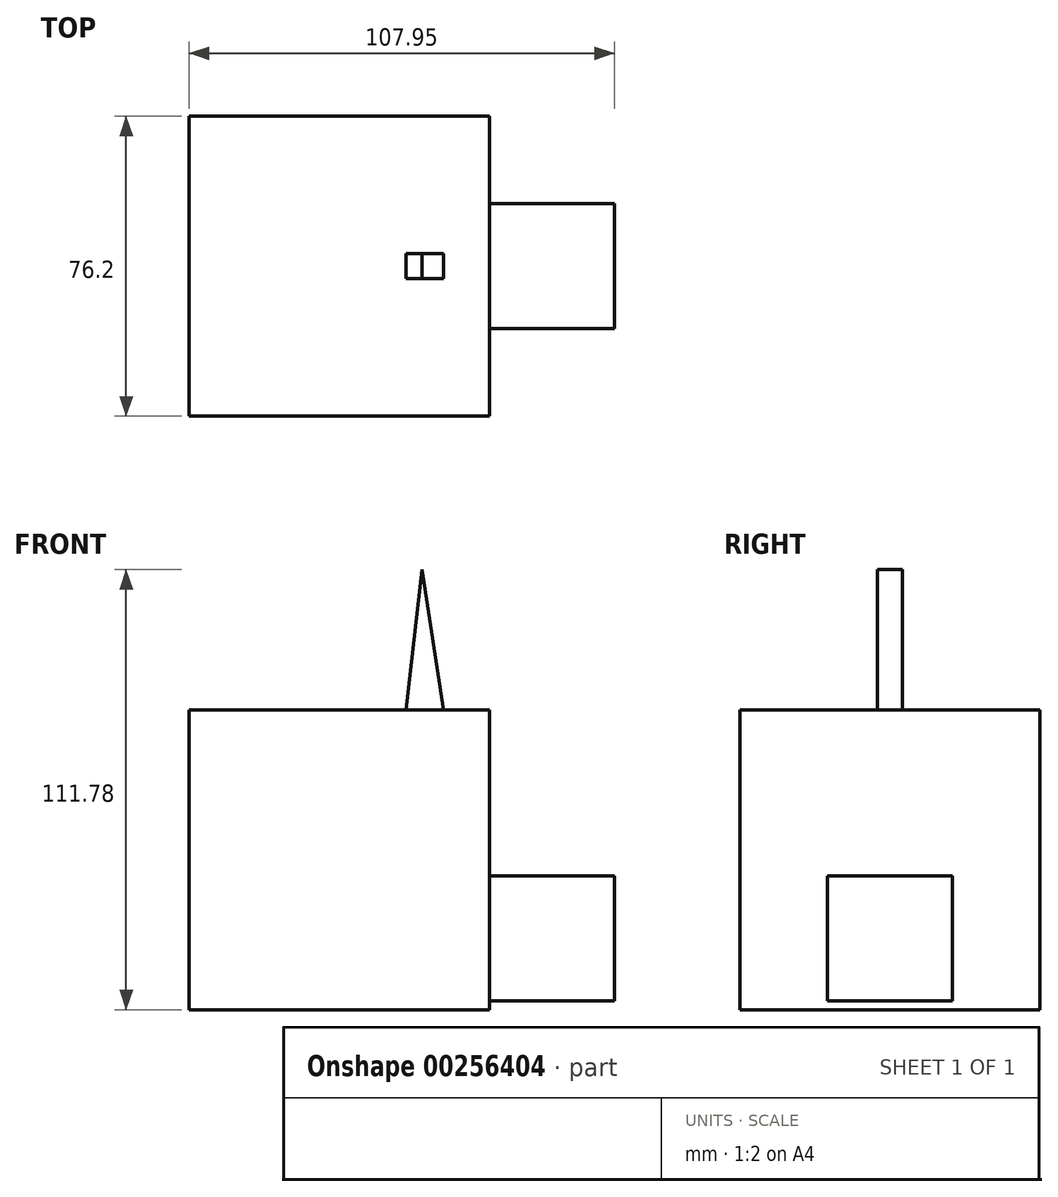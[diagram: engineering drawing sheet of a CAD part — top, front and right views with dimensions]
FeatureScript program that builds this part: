
annotation { "Feature Type Name" : "Feature", "Feature Type Description" : "" }
export const myFeature = defineFeature(function(context is Context, id is Id, definition is map)
    precondition{}
    {
        {
            var Q0;
            Q0=qCreatedBy(makeId("Front.planeOp"),FACE);
            var sketch = newSketch(context, id + "F0", { "sketchPlane" : qUnion([Q0])});
            skLineSegment(sketch, "E0.bottom", {"start": v(38.1, -38.1) * mm, "end": v(-38.1, -38.1) * mm});
            skLineSegment(sketch, "E0.top", {"start": v(38.1, 38.1) * mm, "end": v(-38.1, 38.1) * mm});
            skLineSegment(sketch, "E0.left", {"start": v(38.1, -38.1) * mm, "end": v(38.1, 38.1) * mm});
            skLineSegment(sketch, "E0.right", {"start": v(-38.1, -38.1) * mm, "end": v(-38.1, 38.1) * mm});
            skPoint(sketch, "E0.middle", {"position": v(0, 0) * mm});
            skLineSegment(sketch, "E1", {"start": v(16.94, 38.1) * mm, "end": v(21.02, 73.68) * mm});
            skLineSegment(sketch, "E2", {"start": v(21.02, 73.68) * mm, "end": v(26.53, 38.1) * mm});
            skLineSegment(sketch, "E3.bottom", {"start": v(38.1, -4.17) * mm, "end": v(69.85, -4.17) * mm});
            skLineSegment(sketch, "E3.top", {"start": v(38.1, -35.92) * mm, "end": v(69.85, -35.92) * mm});
            skLineSegment(sketch, "E3.left", {"start": v(38.1, -4.17) * mm, "end": v(38.1, -35.92) * mm});
            skLineSegment(sketch, "E3.right", {"start": v(69.85, -4.17) * mm, "end": v(69.85, -35.92) * mm});
            skSolve(sketch);
        }
        {
            var Q0;
            {var subQ6=sQuery(id+"F0.wireOp",EDGE,"E0.bottom");Q0=makeQuery(id+"F0.imprint","IMPRINT",FACE,{"disambiguationData":[TD([[makeQuery(id+"F0.imprint","IMPRINT",EDGE,{"derivedFrom":subQ6}),-1.0]])]});}
            extrude(context, id + "F1", {"entities" : qUnion([Q0]), "endBound" : BoundingType.SYMMETRIC, "depth" : 76.2 * mm});
        }
        {
            var Q0;
            Q0=makeQuery(id+"F0.imprint","IMPRINT",FACE,{"disambiguationData":[TD([[makeQuery(id+"F0.imprint","IMPRINT",EDGE,{"derivedFrom":sQuery(id+"F0.wireOp",EDGE,"E3.bottom")}),-1.0]])]});
            extrude(context, id + "F2", {"entities" : qUnion([Q0]), "operationType" : NewBodyOperationType.ADD, "endBound" : BoundingType.SYMMETRIC, "depth" : 31.75 * mm});
        }
        {
            var Q0;
            {var subQ0=sQuery(id+"F0.wireOp",EDGE,"E1");Q0=makeQuery(id+"F0.imprint","IMPRINT",FACE,{"disambiguationData":[TD([[makeQuery(id+"F0.imprint","IMPRINT",EDGE,{"derivedFrom":subQ0}),-1.0]])]});}
            extrude(context, id + "F3", {"entities" : qUnion([Q0]), "operationType" : NewBodyOperationType.ADD, "endBound" : BoundingType.SYMMETRIC, "depth" : 6.35 * mm});
        }
    });
